FCSTD DOCUMENT  (FreeCAD 0.20R)
Label: test_group_01
License: Creative Commons Attribution-ShareAlike
LicenseURL: http://creativecommons.org/licenses/by-sa/4.0/
objects: Part::Part2DObjectPython×4, Part::Compound×1, App::DocumentObjectGroup×1
note: 5 computed .brp shape members not serialized (recipe doc carries the construction recipe); baked Part::Feature solids carry a one-line shape summary decoded from their .brp

FEATURE [Part::Part2DObjectPython] Line  label="ln001"  # Draft 2D object (typed FeaturePython)
  Area = 0
  ChamferSize = 0
  Closed = false
  End = (-38.9084,-17.5203,6.11404)
  FilletRadius = 0
  Length = 46.3909
  MakeFace = true
  Placement = pos=(-63.4258,-49.8544,-16.3699) rot=(0.864922,0.231754,0.445197;1.08358rad)
  Points = (2) [(0,0,0),(37.3997,27.4478,-5.94681e-07)]
  Start = (-63.4258,-49.8544,-16.3699)
  Subdivisions = 0
FEATURE [Part::Part2DObjectPython] Line001  label="ln000"  # Draft 2D object (typed FeaturePython)
  Area = 0
  ChamferSize = 0
  Closed = false
  End = (-35.727,-37.477,-20.8404)
  FilletRadius = 0
  Length = 30.6661
  MakeFace = true
  Placement = pos=(-63.4258,-49.8544,-16.3699) rot=(0.864922,0.231754,0.445197;1.08358rad)
  Points = (2) [(0,0,0),(30.1766,-5.45747,-4.17145e-08)]
  Start = (-63.4258,-49.8544,-16.3699)
  Subdivisions = 0
FEATURE [Part::Compound] Compound  label="xc_comp"
  Links = -> [Line001,Line]
FEATURE [Part::Part2DObjectPython] Line002  label="ln002"  # Draft 2D object (typed FeaturePython)
  Area = 0
  ChamferSize = 0
  Closed = false
  End = (19.641,18.627,9.01296)
  FilletRadius = 0
  Length = 53.2762
  MakeFace = true
  Placement = pos=(-12.8145,-17.6375,-12.6638) rot=(0.864922,0.231754,0.445197;1.08358rad)
  Points = (2) [(0,0,0),(46.2396,26.4624,-6.16634e-07)]
  Start = (-12.8145,-17.6375,-12.6638)
  Subdivisions = 0
FEATURE [Part::Part2DObjectPython] Line003  label="ln003"  # Draft 2D object (typed FeaturePython)
  Area = 0
  ChamferSize = 0
  Closed = false
  End = (21.1804,-4.6521,-20.8781)
  FilletRadius = 0
  Length = 37.3061
  MakeFace = true
  Placement = pos=(-12.8145,-17.6375,-12.6638) rot=(0.864922,0.231754,0.445197;1.08358rad)
  Points = (2) [(0,0,0),(35.9331,-10.0279,6.34243e-09)]
  Start = (-12.8145,-17.6375,-12.6638)
  Subdivisions = 0
FEATURE [App::DocumentObjectGroup] Group  label="xc_grp"
  Group = -> [Line002,Line003]
